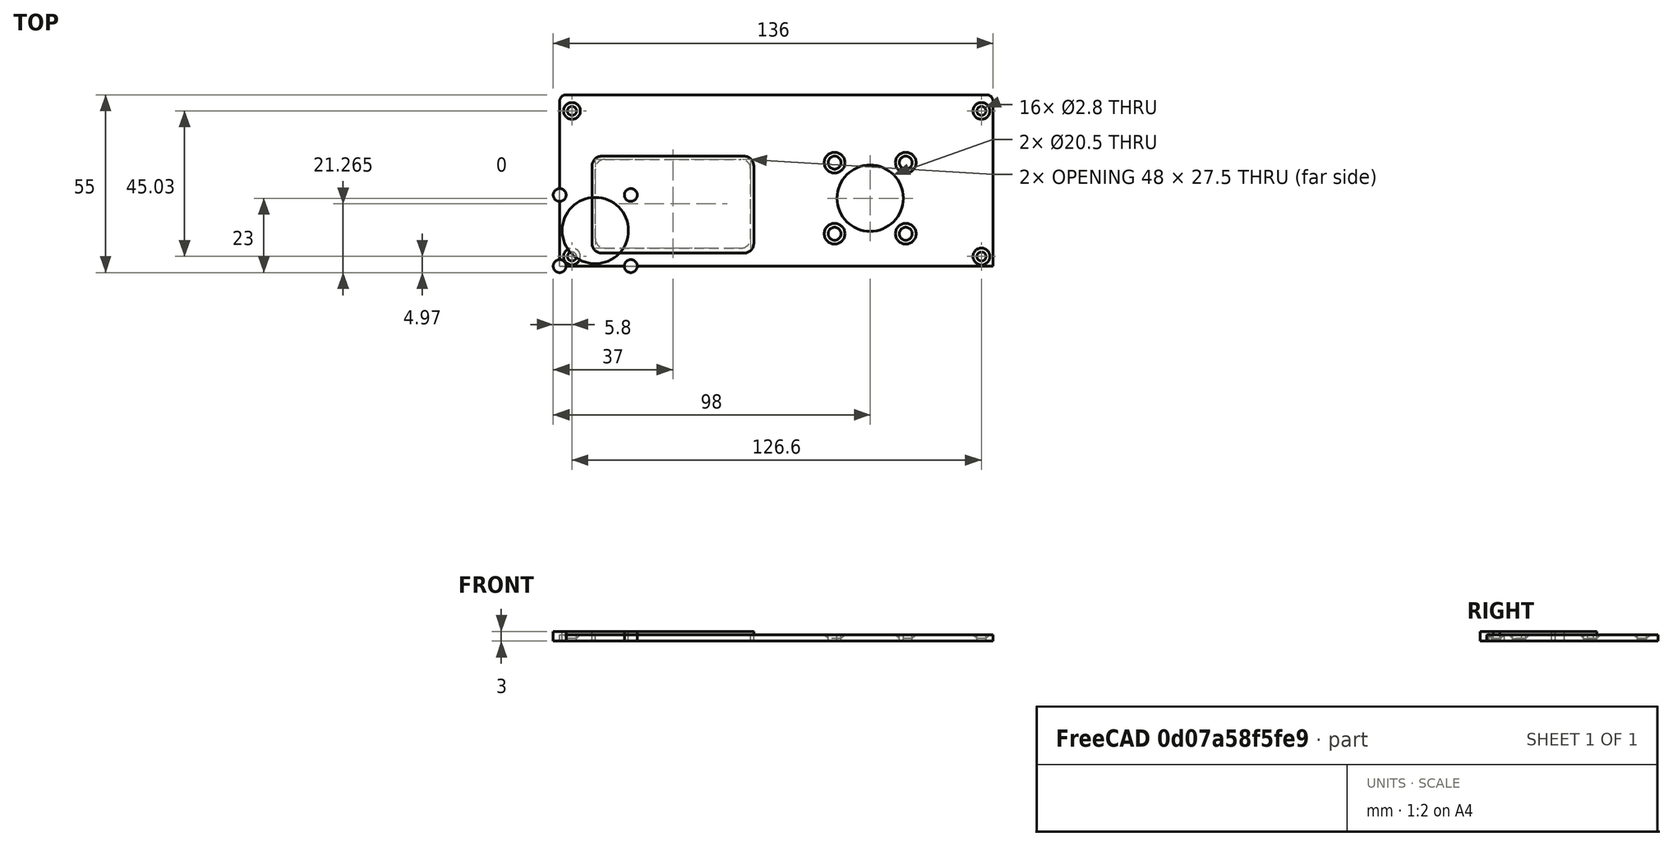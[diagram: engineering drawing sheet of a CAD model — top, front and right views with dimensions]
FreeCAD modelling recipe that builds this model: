
FCSTD DOCUMENT  (FreeCAD 0.17R13522 (Git))
Label: 外壳打样
License: All rights reserved
LicenseURL: http://en.wikipedia.org/wiki/All_rights_reserved
objects: Part::Cylinder×6, Part::Feature×5, Part::Box×3, Part::Fillet×3, Part::Cut×3, Part::MultiFuse×2, Part::Chamfer×2, Part::FeaturePython×1
note: 25 computed .brp shape members not serialized (recipe doc carries the construction recipe); baked Part::Feature solids carry a one-line shape summary decoded from their .brp

FEATURE [Part::Box] Box  label="立方体"
  AttacherType = Attacher::AttachEngine3D
  Height = 2
  Length = 134
  Width = 53
FEATURE [Part::Fillet] Fillet
  Base = -> Box
  Edges = 2 edges r=2: [Edge3,Edge7]
FEATURE [Part::Cylinder] Cylinder  label="圆柱体"
  Angle = 360
  AttacherType = Attacher::AttachEngine3D
  Height = 2
  Placement = pos=(3.8,2.97,0) rot=(0,0,1;0rad)
  Radius = 1.4
FEATURE [Part::Cylinder] Cylinder001  label="圆柱体001"
  Angle = 360
  AttacherType = Attacher::AttachEngine3D
  Height = 2
  Placement = pos=(3.8,48,0) rot=(0,0,1;0rad)
  Radius = 1.4
FEATURE [Part::Cylinder] Cylinder002  label="圆柱体002"
  Angle = 360
  AttacherType = Attacher::AttachEngine3D
  Height = 2
  Placement = pos=(130.4,2.97,0) rot=(0,0,1;0rad)
  Radius = 1.4
FEATURE [Part::Cylinder] Cylinder003  label="圆柱体003"
  Angle = 360
  AttacherType = Attacher::AttachEngine3D
  Height = 2
  Placement = pos=(130.4,48,0) rot=(0,0,1;0rad)
  Radius = 1.4
FEATURE [Part::MultiFuse] Fusion
  Shapes = -> [Cylinder,Cylinder003,Cylinder001,Cylinder002]
FEATURE [Part::Cut] Cut
  Base = -> Fillet
  Tool = -> Fusion
FEATURE [Part::Feature] Cut001
  shape: bbox 134 x 53 x 2 mm, 12 faces (baked)
FEATURE [Part::Chamfer] Chamfer
  Base = -> Cut001
  Edges = 4 edges r=1.2: [Edge10,Edge11,Edge12,Edge13]
FEATURE [Part::Box] Box001  label="立方体001"
  AttacherType = Attacher::AttachEngine3D
  Height = 2
  Length = 48
  Width = 27.5
FEATURE [Part::Fillet] Fillet001
  Base = -> Box001
  Edges = 4 edges r=3: [Edge1,Edge3,Edge5,Edge7]
  Placement = pos=(11,5.515,0) rot=(0,0,1;0rad)
FEATURE [Part::Box] Box002  label="立方体002"
  AttacherType = Attacher::AttachEngine3D
  Height = 3
  Length = 50
  Width = 30
FEATURE [Part::Fillet] Fillet002
  Base = -> Box002
  Edges = 4 edges r=3: [Edge1,Edge3,Edge5,Edge7]
  Placement = pos=(10,4,0) rot=(0,0,1;0rad)
FEATURE [Part::Cylinder] Cylinder004  label="圆柱体004"
  Angle = 360
  AttacherType = Attacher::AttachEngine3D
  Height = 3
  Radius = 2
FEATURE [Part::FeaturePython] Array  # Draft array (typed FeaturePython)
  Angle = 360
  ArrayType = 0
  Axis = (0,0,1)
  Base = -> Cylinder004
  Center = (0,0,0)
  Fuse = false
  IntervalAxis = (0,0,0)
  IntervalX = (22,0,0)
  IntervalY = (0,22,0)
  IntervalZ = (0,0,0)
  NumberPolar = 1
  NumberX = 2
  NumberY = 2
  NumberZ = 1
FEATURE [Part::Cylinder] Cylinder005  label="圆柱体005"
  Angle = 360
  AttacherType = Attacher::AttachEngine3D
  Height = 3
  Placement = pos=(11,11,0) rot=(0,0,1;0rad)
  Radius = 10.25
FEATURE [Part::MultiFuse] Fusion001
  Shapes = -> [Cylinder005,Array]
FEATURE [Part::Feature] Fusion001001  label="Fusion002"
  Placement = pos=(85,10,0) rot=(0,0,1;0rad)
  shape: bbox 26 x 26 x 3 mm, 15 faces, 5 solids (baked)
FEATURE [Part::Feature] Fillet001001  label="Fillet003"
  Placement = pos=(11,5.515,0) rot=(0,0,1;0rad)
  shape: bbox 48 x 27.5 x 2 mm, 10 faces (baked)
FEATURE [Part::Feature] Chamfer001
  shape: bbox 134 x 53 x 2 mm, 16 faces (baked)
FEATURE [Part::Cut] Cut002
  Base = -> Chamfer001
  Tool = -> Fillet001001
FEATURE [Part::Cut] Cut003
  Base = -> Cut002
  Tool = -> Fusion001001
FEATURE [Part::Feature] Cut003001  label="Cut004"
  shape: bbox 134 x 53 x 2 mm, 29 faces (baked)
FEATURE [Part::Chamfer] Chamfer002
  Base = -> Cut003001
  Edges = 4 edges r=1.2: [Edge15,Edge16,Edge17,Edge19]
